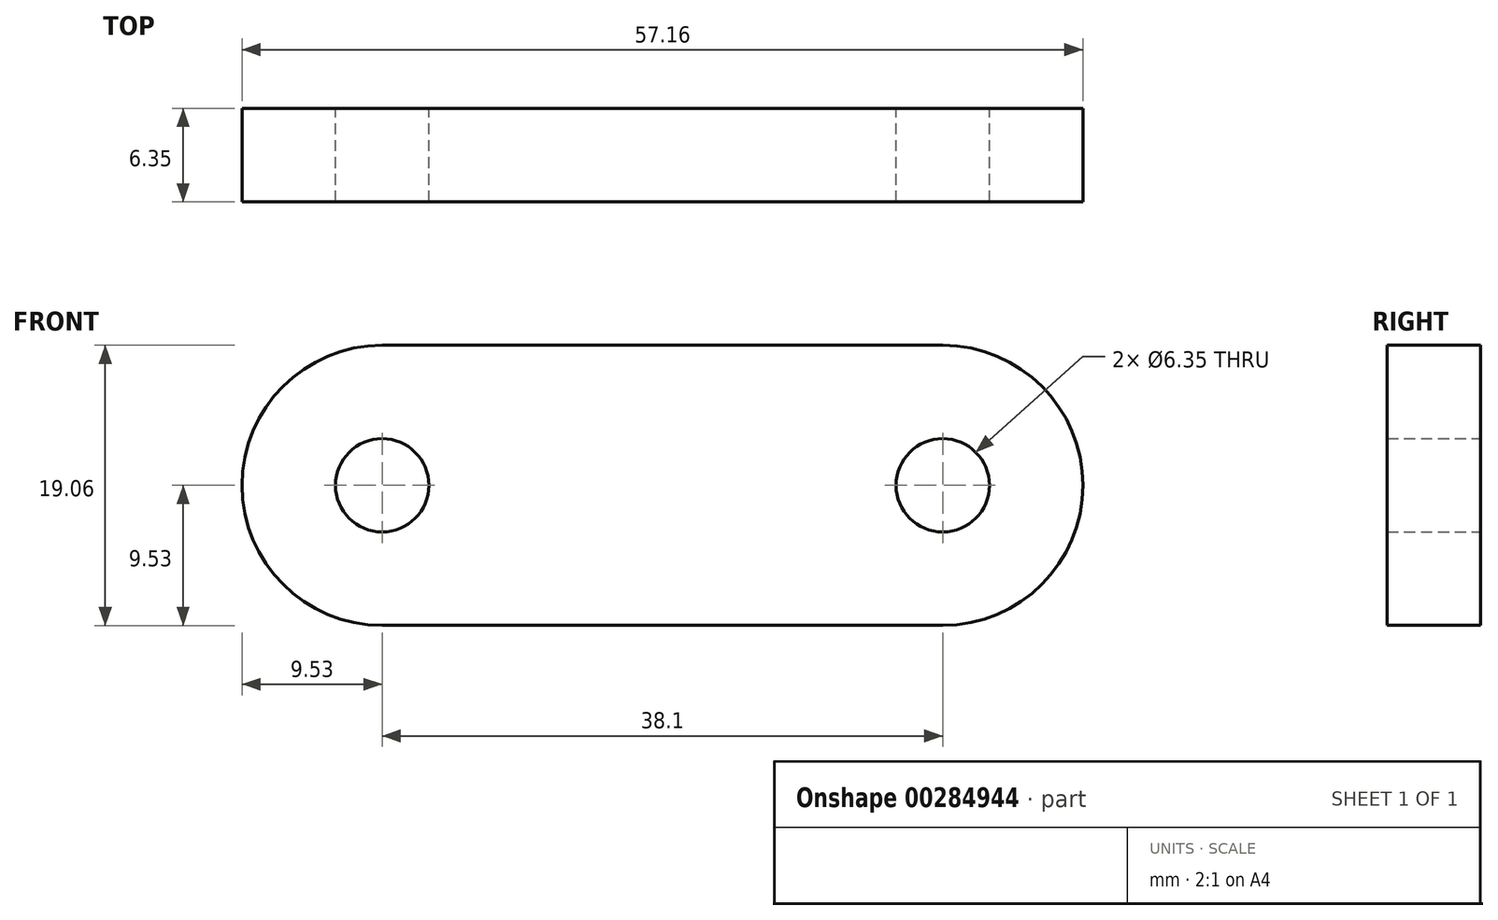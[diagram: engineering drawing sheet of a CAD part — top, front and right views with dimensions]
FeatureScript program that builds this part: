
annotation { "Feature Type Name" : "Feature", "Feature Type Description" : "" }
export const myFeature = defineFeature(function(context is Context, id is Id, definition is map)
    precondition{}
    {
        {
            var Q0;
            Q0=qCreatedBy(makeId("Front.planeOp"),FACE);
            var sketch = newSketch(context, id + "F0", { "sketchPlane" : qUnion([Q0])});
            skLineSegment(sketch, "E0.bottom", {"start": v(19.05, 9.52) * mm, "end": v(-19.05, 9.52) * mm});
            skLineSegment(sketch, "E0.top", {"start": v(19.05, -9.53) * mm, "end": v(-19.05, -9.53) * mm});
            skPoint(sketch, "E0.middle", {"position": v(0, 0) * mm});
            skArc(sketch, "E1", {"start": v(-19.05, 9.52) * mm, "mid": v(-28.58, 0) * mm, "end": v(-19.05, -9.53) * mm});
            skArc(sketch, "E2", {"start": v(19.05, -9.53) * mm, "mid": v(28.58, 0) * mm, "end": v(19.05, 9.52) * mm});
            skCircle(sketch, "E3", {"center": v(-19.05, 0) * mm, "radius": 3.18 * mm});
            skCircle(sketch, "E4", {"center": v(19.05, 0) * mm, "radius": 3.18 * mm});
            skSolve(sketch);
        }
        {
            var Q0;
            Q0=makeQuery(id+"F0.imprint","IMPRINT",FACE,{"disambiguationData":[TD([[makeQuery(id+"F0.imprint","IMPRINT",EDGE,{"derivedFrom":sQuery(id+"F0.wireOp",EDGE,"E0.bottom")}),1.0]])]});
            extrude(context, id + "F1", {"entities" : qUnion([Q0]), "depth" : 6.35 * mm});
        }
    });
